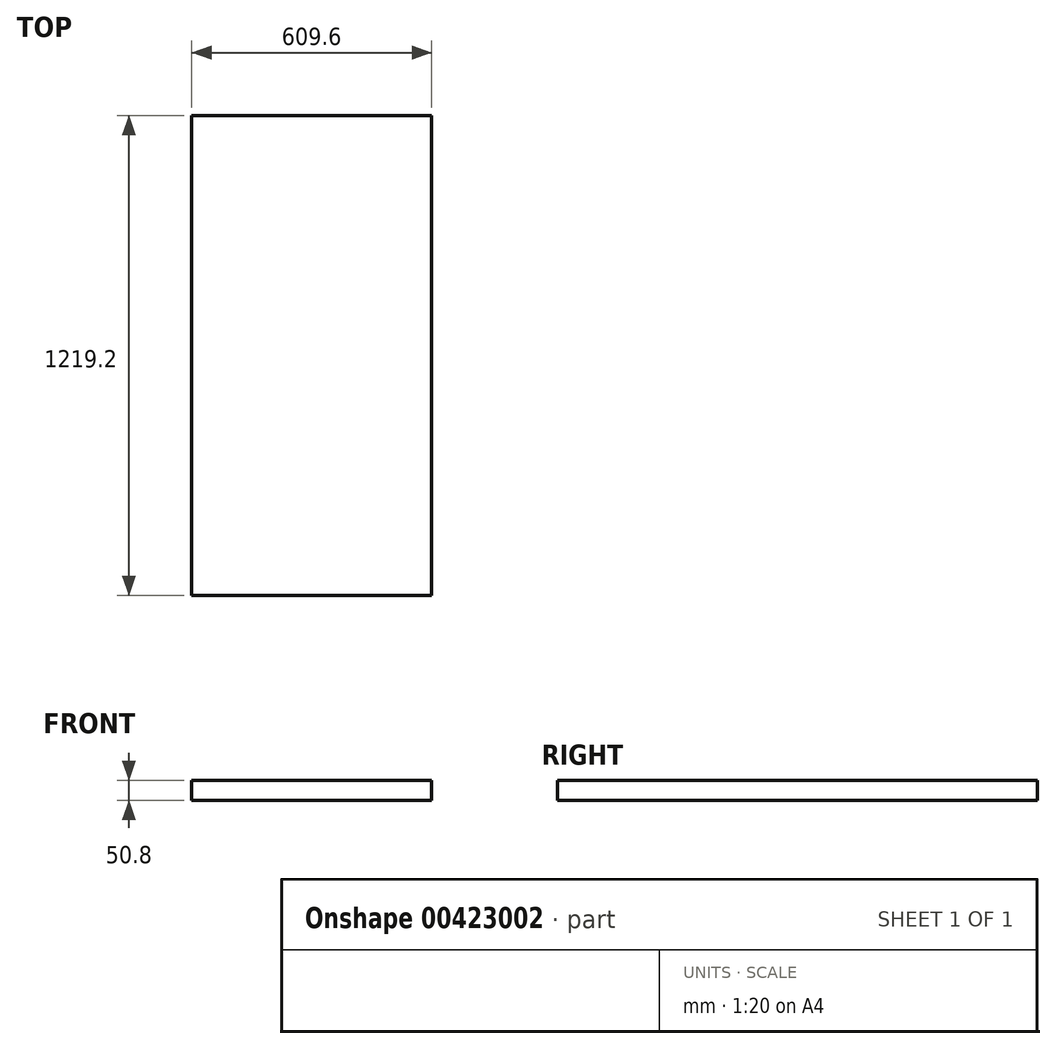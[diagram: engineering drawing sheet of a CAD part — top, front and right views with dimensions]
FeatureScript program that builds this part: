
annotation { "Feature Type Name" : "Feature", "Feature Type Description" : "" }
export const myFeature = defineFeature(function(context is Context, id is Id, definition is map)
    precondition{}
    {
        {
            var Q0;
            Q0=qCreatedBy(makeId("Top.planeOp"),FACE);
            var sketch = newSketch(context, id + "F0", { "sketchPlane" : qUnion([Q0])});
            skLineSegment(sketch, "E0.bottom", {"start": v(304.8, -609.6) * mm, "end": v(-304.8, -609.6) * mm});
            skLineSegment(sketch, "E0.top", {"start": v(304.8, 609.6) * mm, "end": v(-304.8, 609.6) * mm});
            skLineSegment(sketch, "E0.left", {"start": v(304.8, -609.6) * mm, "end": v(304.8, 609.6) * mm});
            skLineSegment(sketch, "E0.right", {"start": v(-304.8, -609.6) * mm, "end": v(-304.8, 609.6) * mm});
            skPoint(sketch, "E0.middle", {"position": v(0, 0) * mm});
            skSolve(sketch);
        }
        {
            var Q0;
            Q0 = qSketchRegion(id + "F0", true);
            extrude(context, id + "F1", {"entities" : qUnion([Q0]), "depth" : 50.8 * mm});
        }
    });
